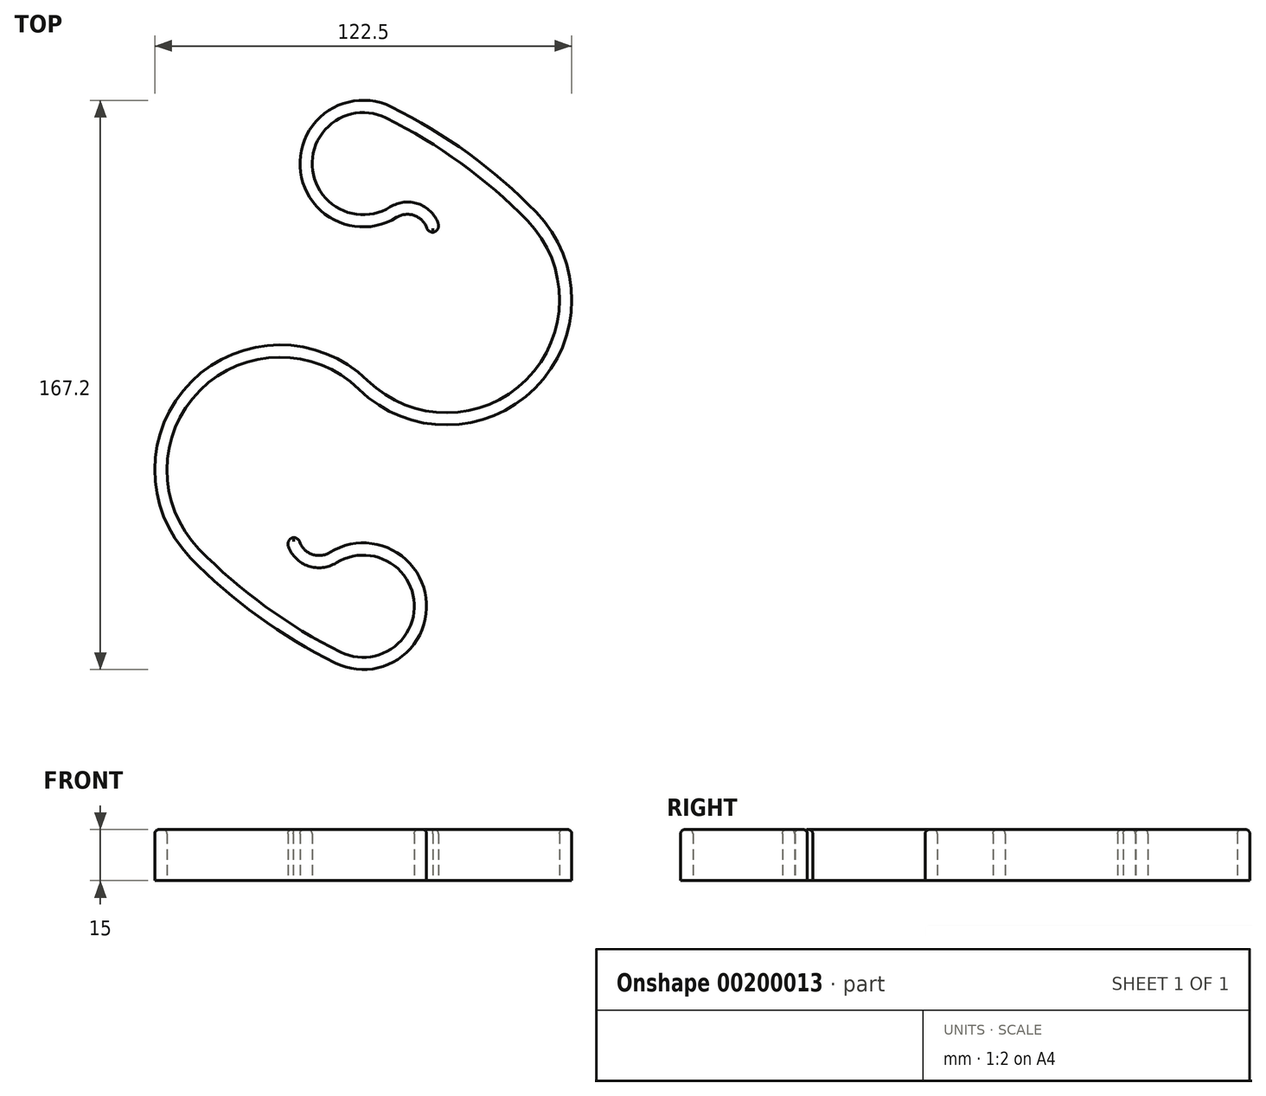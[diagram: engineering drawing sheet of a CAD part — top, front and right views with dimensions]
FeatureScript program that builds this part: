
annotation { "Feature Type Name" : "Feature", "Feature Type Description" : "" }
export const myFeature = defineFeature(function(context is Context, id is Id, definition is map)
    precondition{}
    {
        {
            var Q0;
            Q0=qCreatedBy(makeId("Top.planeOp"),FACE);
            var sketch = newSketch(context, id + "F0", { "sketchPlane" : qUnion([Q0])});
            skLineSegment(sketch, "E0", {"start": v(0, 65) * mm, "end": v(0, -65) * mm, "construction": true});
            skArc(sketch, "E1", {"start": v(7.45, 80.06) * mm, "mid": v(-16.78, 64.18) * mm, "end": v(8.88, 50.74) * mm, "construction": true});
            skArc(sketch, "E2", {"start": v(-7.45, -80.06) * mm, "mid": v(16.78, -64.18) * mm, "end": v(-8.88, -50.74) * mm, "construction": true});
            skLineSegment(sketch, "E3", {"start": v(0, 0) * mm, "end": v(49.5, 49.5) * mm, "construction": true});
            skLineSegment(sketch, "E4", {"start": v(0, 0) * mm, "end": v(-49.5, -49.5) * mm, "construction": true});
            skArc(sketch, "E5", {"start": v(49.5, 49.5) * mm, "mid": v(29.77, 66.56) * mm, "end": v(7.45, 80.06) * mm, "construction": true});
            skArc(sketch, "E6", {"start": v(49.5, 49.5) * mm, "mid": v(49.2, 0.3) * mm, "end": v(0, 0) * mm, "construction": true});
            skArc(sketch, "E7", {"start": v(0, 0) * mm, "mid": v(-49.2, -0.3) * mm, "end": v(-49.5, -49.5) * mm, "construction": true});
            skArc(sketch, "E8", {"start": v(-49.5, -49.5) * mm, "mid": v(-29.77, -66.56) * mm, "end": v(-7.45, -80.06) * mm, "construction": true});
            skLineSegment(sketch, "E9", {"start": v(-8.88, -50.74) * mm, "end": v(-7.45, -80.06) * mm, "construction": true});
            skLineSegment(sketch, "E10", {"start": v(8.88, 50.74) * mm, "end": v(7.45, 80.06) * mm, "construction": true});
            skArc(sketch, "E11.0", {"start": v(6.65, 78.44) * mm, "mid": v(-14.98, 64.27) * mm, "end": v(7.93, 52.26) * mm});
            skArc(sketch, "E11.1", {"start": v(48.2, 48.24) * mm, "mid": v(28.71, 65.1) * mm, "end": v(6.65, 78.44) * mm});
            skArc(sketch, "E11.2", {"start": v(-8.25, -81.67) * mm, "mid": v(18.58, -64.1) * mm, "end": v(-9.83, -49.2) * mm});
            skArc(sketch, "E11.3", {"start": v(-50.79, -50.75) * mm, "mid": v(-30.83, -68.02) * mm, "end": v(-8.25, -81.67) * mm});
            skArc(sketch, "E11.4", {"start": v(1.26, 1.29) * mm, "mid": v(-50.47, 0.97) * mm, "end": v(-50.79, -50.75) * mm});
            skArc(sketch, "E11.5", {"start": v(48.2, 48.24) * mm, "mid": v(47.93, 1.57) * mm, "end": v(1.26, 1.29) * mm});
            skArc(sketch, "E12.0", {"start": v(8.25, 81.67) * mm, "mid": v(-18.58, 64.1) * mm, "end": v(9.83, 49.2) * mm});
            skArc(sketch, "E12.1", {"start": v(50.79, 50.75) * mm, "mid": v(30.83, 68.02) * mm, "end": v(8.25, 81.67) * mm});
            skArc(sketch, "E12.2", {"start": v(-6.65, -78.44) * mm, "mid": v(14.98, -64.27) * mm, "end": v(-7.93, -52.26) * mm});
            skArc(sketch, "E12.3", {"start": v(-48.2, -48.24) * mm, "mid": v(-28.71, -65.1) * mm, "end": v(-6.65, -78.44) * mm});
            skArc(sketch, "E12.4", {"start": v(-1.26, -1.29) * mm, "mid": v(-47.93, -1.57) * mm, "end": v(-48.2, -48.24) * mm});
            skArc(sketch, "E12.5", {"start": v(50.79, 50.75) * mm, "mid": v(50.47, -0.97) * mm, "end": v(-1.26, -1.29) * mm});
            skArc(sketch, "E13", {"start": v(8.88, 50.74) * mm, "mid": v(16.48, 51.1) * mm, "end": v(20.77, 44.8) * mm, "construction": true});
            skArc(sketch, "E14.0", {"start": v(7.93, 52.26) * mm, "mid": v(17.28, 52.7) * mm, "end": v(22.56, 44.97) * mm});
            skArc(sketch, "E15.0", {"start": v(9.83, 49.2) * mm, "mid": v(15.68, 49.48) * mm, "end": v(18.97, 44.65) * mm});
            skLineSegment(sketch, "E16", {"start": v(22.56, 44.97) * mm, "end": v(18.97, 44.65) * mm});
            skArc(sketch, "E17", {"start": v(-8.88, -50.74) * mm, "mid": v(-16.48, -51.1) * mm, "end": v(-20.77, -44.8) * mm, "construction": true});
            skArc(sketch, "E18", {"start": v(-9.83, -49.2) * mm, "mid": v(-15.68, -49.48) * mm, "end": v(-18.97, -44.65) * mm});
            skArc(sketch, "E19", {"start": v(-7.93, -52.26) * mm, "mid": v(-17.28, -52.7) * mm, "end": v(-22.56, -44.97) * mm});
            skLineSegment(sketch, "E20", {"start": v(-18.97, -44.65) * mm, "end": v(-22.56, -44.97) * mm});
            skLineSegment(sketch, "E21", {"start": v(18.97, 44.65) * mm, "end": v(9.83, 49.2) * mm, "construction": true});
            skLineSegment(sketch, "E22", {"start": v(-9.83, -49.2) * mm, "end": v(-18.97, -44.65) * mm, "construction": true});
            skCircle(sketch, "E23", {"center": v(0, 0) * mm, "radius": 70 * mm, "construction": true});
            skSolve(sketch);
        }
        {
            var Q0;
            Q0 = qSketchRegion(id + "F0", true);
            extrude(context, id + "F1", {"entities" : qUnion([Q0]), "endBound" : BoundingType.SYMMETRIC, "depth" : 15 * mm});
        }
        {
            var Q0;
            Q0=makeQuery(id+"F1.opExtrude","SWEPT_EDGE",EDGE,{"disambiguationData":[OSD([sQuery(id+"F0.wireOp",EDGE,"E14.0"),sQuery(id+"F0.wireOp",EDGE,"E16")])]});
            var Q1;
            Q1=makeQuery(id+"F1.opExtrude","SWEPT_EDGE",EDGE,{"disambiguationData":[OSD([sQuery(id+"F0.wireOp",EDGE,"E15.0"),sQuery(id+"F0.wireOp",EDGE,"E16")])]});
            var Q2;
            Q2=makeQuery(id+"F1.opExtrude","SWEPT_EDGE",EDGE,{"disambiguationData":[OSD([sQuery(id+"F0.wireOp",EDGE,"E18"),sQuery(id+"F0.wireOp",EDGE,"E20")])]});
            var Q3;
            Q3=makeQuery(id+"F1.opExtrude","SWEPT_EDGE",EDGE,{"disambiguationData":[OSD([sQuery(id+"F0.wireOp",EDGE,"E19"),sQuery(id+"F0.wireOp",EDGE,"E20")])]});
            fillet(context, id + "F2", {"entities" : qUnion([Q0, Q1, Q2, Q3]), "radius" : 2 * mm, "tangentPropagation" : true, "allowEdgeOverflow" : false});
        }
        {
            var Q0;
            Q0=makeQuery(id+"F1.opExtrude","CAP_EDGE",EDGE,{"disambiguationData":[OSD([sQuery(id+"F0.wireOp",EDGE,"E12.4")])],"isStart":false});
            var Q1;
            Q1=makeQuery(id+"F1.opExtrude","CAP_EDGE",EDGE,{"disambiguationData":[OSD([sQuery(id+"F0.wireOp",EDGE,"E11.4")])],"isStart":false});
            fillet(context, id + "F3", {"entities" : qUnion([Q0, Q1]), "radius" : 1.2 * mm, "tangentPropagation" : true, "allowEdgeOverflow" : false});
        }
    });
